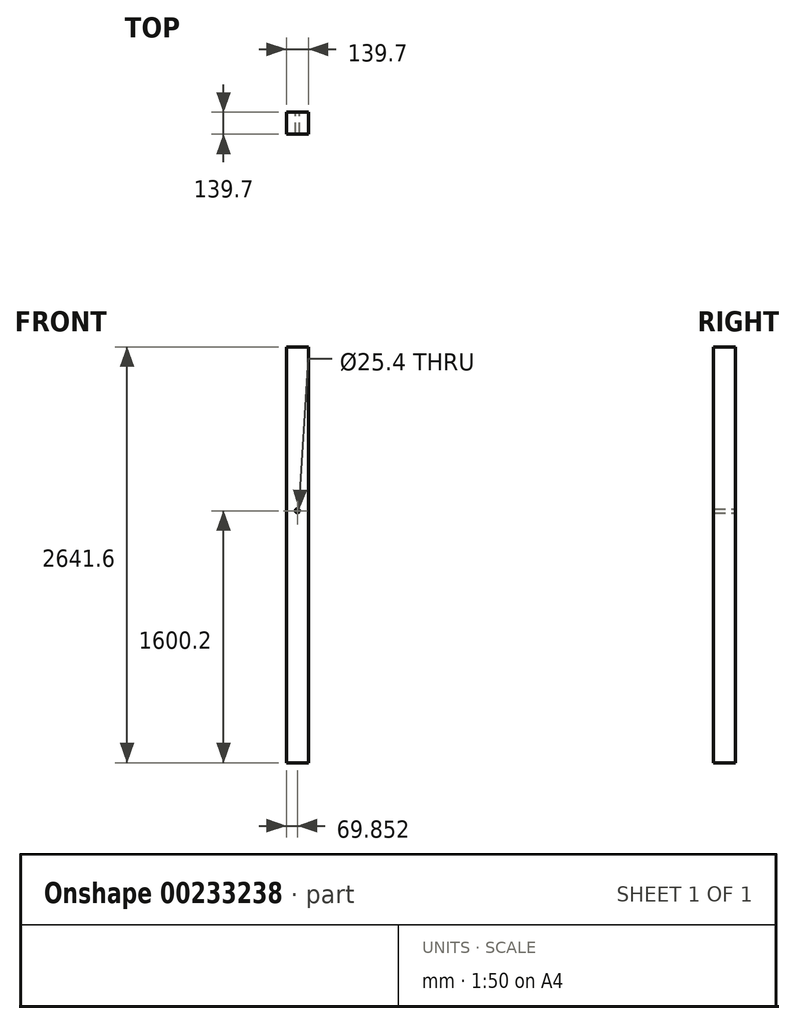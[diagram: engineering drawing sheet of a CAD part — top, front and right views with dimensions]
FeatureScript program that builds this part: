
annotation { "Feature Type Name" : "Feature", "Feature Type Description" : "" }
export const myFeature = defineFeature(function(context is Context, id is Id, definition is map)
    precondition{}
    {
        {
            var Q0;
            Q0=qCreatedBy(makeId("Front.planeOp"),FACE);
            var sketch = newSketch(context, id + "F0", { "sketchPlane" : qUnion([Q0])});
            skLineSegment(sketch, "E0.bottom", {"start": v(157.77, 2603.02) * mm, "end": v(297.47, 2603.02) * mm});
            skLineSegment(sketch, "E0.top", {"start": v(157.77, -38.58) * mm, "end": v(297.47, -38.58) * mm});
            skLineSegment(sketch, "E0.left", {"start": v(157.77, 2603.02) * mm, "end": v(157.77, -38.58) * mm});
            skLineSegment(sketch, "E0.right", {"start": v(297.47, 2603.02) * mm, "end": v(297.47, -38.58) * mm});
            skCircle(sketch, "E1", {"center": v(227.62, 1561.62) * mm, "radius": 12.7 * mm});
            skSolve(sketch);
        }
        {
            var Q0;
            Q0=makeQuery(id+"F0.imprint","IMPRINT",FACE,{"disambiguationData":[TD([[makeQuery(id+"F0.imprint","IMPRINT",EDGE,{"derivedFrom":sQuery(id+"F0.wireOp",EDGE,"E0.bottom")}),-1.0]])]});
            extrude(context, id + "F1", {"entities" : qUnion([Q0]), "depth" : 139.7 * mm});
        }
    });
